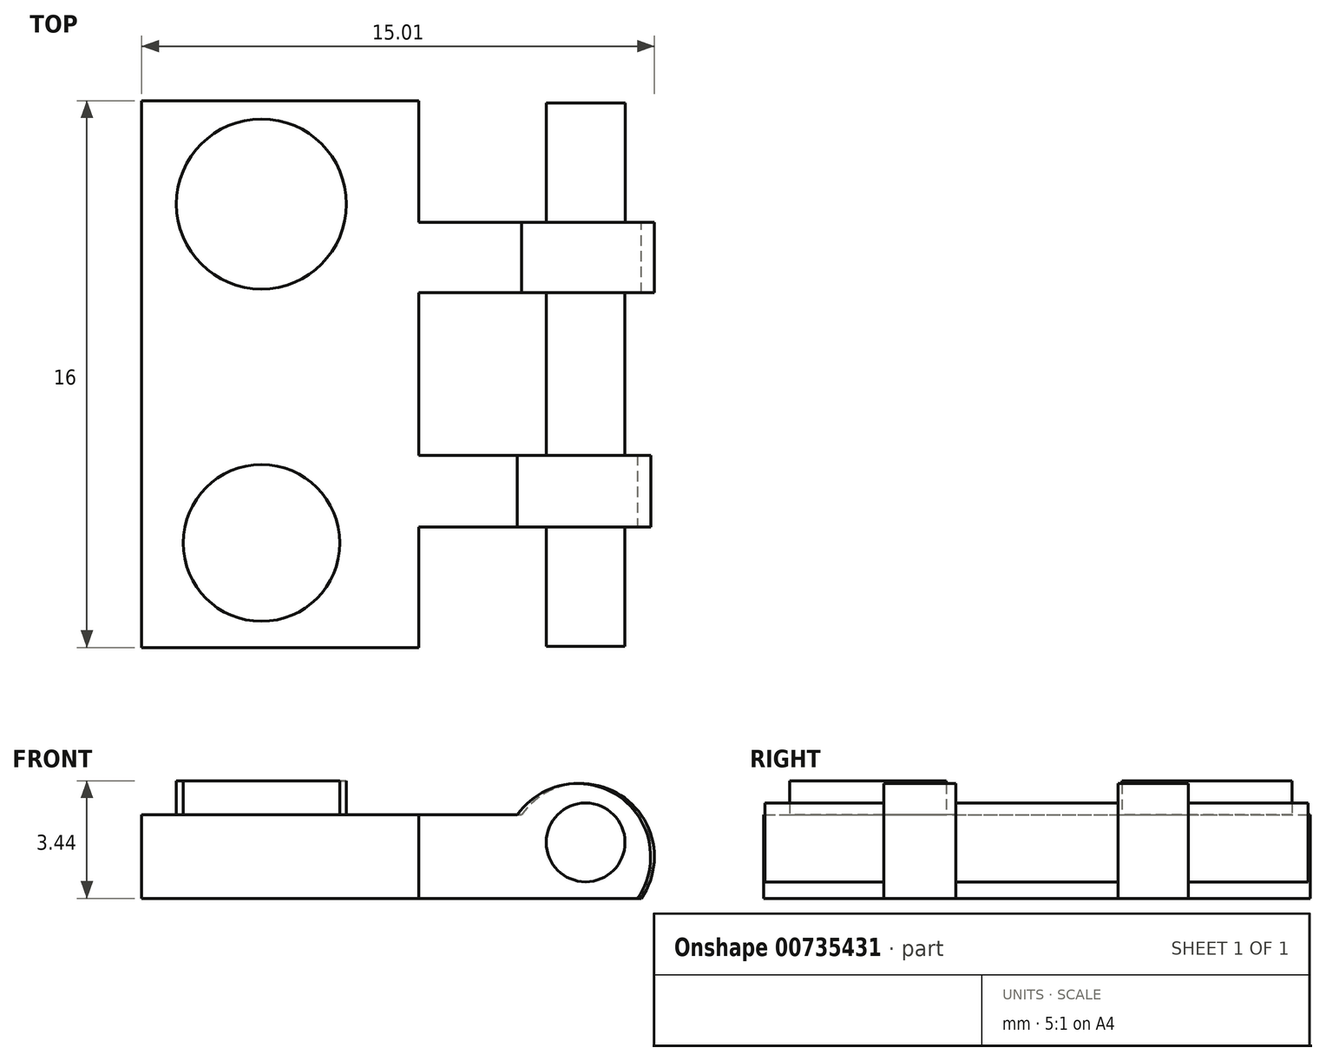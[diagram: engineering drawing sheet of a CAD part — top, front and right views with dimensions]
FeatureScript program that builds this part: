
annotation { "Feature Type Name" : "Feature", "Feature Type Description" : "" }
export const myFeature = defineFeature(function(context is Context, id is Id, definition is map)
    precondition{}
    {
        {
            var Q0;
            Q0=qCreatedBy(makeId("Front.planeOp"),FACE);
            var sketch = newSketch(context, id + "F0", { "sketchPlane" : qUnion([Q0])});
            skLineSegment(sketch, "E0", {"start": v(0, 0) * mm, "end": v(0, 2.44) * mm});
            skLineSegment(sketch, "E1", {"start": v(0, 2.44) * mm, "end": v(8.1, 2.44) * mm});
            skLineSegment(sketch, "E2", {"start": v(8.1, 2.44) * mm, "end": v(8.1, 0) * mm});
            skLineSegment(sketch, "E3", {"start": v(8.1, 0) * mm, "end": v(0, 0) * mm});
            skSolve(sketch);
        }
        {
            var Q0;
            Q0 = qSketchRegion(id + "F0", true);
            extrude(context, id + "F1", {"entities" : qUnion([Q0]), "depth" : 16 * mm, "offsetDistance" : 25 * mm});
        }
        {
            var Q0;
            Q0=makeQuery(id+"F1.opExtrude","SWEPT_FACE",FACE,{"disambiguationData":[OSD([sQuery(id+"F0.wireOp",EDGE,"E2")])]});
            var sketch = newSketch(context, id + "F2", { "sketchPlane" : qUnion([Q0])});
            skLineSegment(sketch, "E4", {"start": v(-12.48, 2.44) * mm, "end": v(-10.37, 2.44) * mm});
            skLineSegment(sketch, "E5", {"start": v(-3.56, 2.44) * mm, "end": v(-5.62, 2.44) * mm});
            skLineSegment(sketch, "E6", {"start": v(-12.48, 2.44) * mm, "end": v(-12.48, 0) * mm});
            skLineSegment(sketch, "E7", {"start": v(-12.48, 0) * mm, "end": v(-10.37, 0) * mm});
            skLineSegment(sketch, "E8", {"start": v(-10.37, 0) * mm, "end": v(-10.37, 2.44) * mm});
            skLineSegment(sketch, "E9", {"start": v(-5.62, 2.44) * mm, "end": v(-5.62, 0) * mm});
            skLineSegment(sketch, "E10", {"start": v(-5.62, 0) * mm, "end": v(-3.56, 0) * mm});
            skLineSegment(sketch, "E11", {"start": v(-3.56, 0) * mm, "end": v(-3.56, 2.44) * mm});
            skSolve(sketch);
        }
        {
            var Q0;
            Q0 = qSketchRegion(id + "F2", true);
            extrude(context, id + "F3", {"entities" : qUnion([Q0]), "operationType" : NewBodyOperationType.ADD, "depth" : 2.5 * mm, "offsetDistance" : 25 * mm});
        }
        {
            var Q0;
            Q0=makeQuery(id+"F3.opExtrude","SWEPT_FACE",FACE,{"disambiguationData":[OSD([sQuery(id+"F2.wireOp",EDGE,"E6")])]});
            var sketch = newSketch(context, id + "F4", { "sketchPlane" : qUnion([Q0])});
            skPoint(sketch, "E12.endSnap0", {"position": v(10.6, 1.22) * mm});
            skArc(sketch, "E13", {"start": v(14.52, 0) * mm, "mid": v(13.98, 2.98) * mm, "end": v(11, 2.44) * mm});
            skLineSegment(sketch, "E14", {"start": v(10.6, 0) * mm, "end": v(14.52, 0) * mm});
            skLineSegment(sketch, "E15", {"start": v(10.6, 2.44) * mm, "end": v(11, 2.44) * mm});
            skSolve(sketch);
        }
        {
            var Q0;
            Q0 = qSketchRegion(id + "F4", true);
            var Q1;
            Q1=makeQuery(id+"F4.imprint","IMPRINT",FACE,{"disambiguationData":[TD([[makeQuery(id+"F4.imprint","IMPRINT",EDGE,{"derivedFrom":sQuery(id+"F4.wireOp",EDGE,"E13")}),1.0]])]});
            extrude(context, id + "F5", {"entities" : qUnion([Q0, Q1]), "operationType" : NewBodyOperationType.ADD, "oppositeDirection" : true, "depth" : 2.1 * mm, "offsetDistance" : 25 * mm});
        }
        {
            var Q0;
            Q0=makeQuery(id+"F3.opExtrude","SWEPT_FACE",FACE,{"disambiguationData":[OSD([sQuery(id+"F2.wireOp",EDGE,"E11")])]});
            var sketch = newSketch(context, id + "F6", { "sketchPlane" : qUnion([Q0])});
            skPoint(sketch, "E16.endSnap0", {"position": v(8.94, -90.2) * mm});
            skArc(sketch, "E17", {"start": v(12.86, -91.43) * mm, "mid": v(12.32, -88.45) * mm, "end": v(9.34, -88.99) * mm});
            skLineSegment(sketch, "E18", {"start": v(8.94, -91.43) * mm, "end": v(12.86, -91.43) * mm});
            skLineSegment(sketch, "E19", {"start": v(8.94, -88.99) * mm, "end": v(9.34, -88.99) * mm});
            skArc(sketch, "E20", {"start": v(-11.12, 2.44) * mm, "mid": v(-14.1, 2.97) * mm, "end": v(-14.63, 0) * mm});
            skLineSegment(sketch, "E21", {"start": v(-10.6, 0) * mm, "end": v(-14.63, 0) * mm});
            skLineSegment(sketch, "E22", {"start": v(-10.6, 2.44) * mm, "end": v(-11.12, 2.44) * mm});
            skLineSegment(sketch, "E23", {"start": v(-10.6, 2.44) * mm, "end": v(-10.6, 0) * mm});
            skSolve(sketch);
        }
        {
            var Q0;
            Q0 = qSketchRegion(id + "F6", true);
            extrude(context, id + "F7", {"entities" : qUnion([Q0]), "operationType" : NewBodyOperationType.ADD, "oppositeDirection" : true, "depth" : 2.06 * mm, "offsetDistance" : 25 * mm});
        }
        {
            var Q0;
            Q0=makeQuery(id+"F7.boolean.opBoolean","MERGE",FACE,{"derivedFrom":[makeQuery(id+"F3.opExtrude","SWEPT_FACE",FACE,{"disambiguationData":[OSD([sQuery(id+"F2.wireOp",EDGE,"E11")])]}),makeQuery(id+"F7.opExtrude","CAP_FACE",FACE,{"disambiguationData":[OSD([sQuery(id+"F6.wireOp",EDGE,"E20"),sQuery(id+"F6.wireOp",EDGE,"E21"),sQuery(id+"F6.wireOp",EDGE,"E22"),sQuery(id+"F6.wireOp",EDGE,"E23")])],"isStart":true})]});
            var sketch = newSketch(context, id + "F8", { "sketchPlane" : qUnion([Q0])});
            skCircle(sketch, "E24", {"center": v(-13, 1.64) * mm, "radius": 1.16 * mm});
            skSolve(sketch);
        }
        {
            var Q0;
            Q0 = qSketchRegion(id + "F8", true);
            extrude(context, id + "F9", {"entities" : qUnion([Q0]), "operationType" : NewBodyOperationType.ADD, "depth" : 3.5 * mm, "offsetDistance" : 25 * mm});
        }
        {
            var Q0;
            Q0=makeQuery(id+"F7.boolean.opBoolean","MERGE",FACE,{"derivedFrom":[makeQuery(id+"F3.opExtrude","SWEPT_FACE",FACE,{"disambiguationData":[OSD([sQuery(id+"F2.wireOp",EDGE,"E11")])]}),makeQuery(id+"F7.opExtrude","CAP_FACE",FACE,{"disambiguationData":[OSD([sQuery(id+"F6.wireOp",EDGE,"E20"),sQuery(id+"F6.wireOp",EDGE,"E21"),sQuery(id+"F6.wireOp",EDGE,"E22"),sQuery(id+"F6.wireOp",EDGE,"E23")])],"isStart":true})]});
            var sketch = newSketch(context, id + "F10", { "sketchPlane" : qUnion([Q0])});
            skCircle(sketch, "E25", {"center": v(-13, 1.64) * mm, "radius": 1.15 * mm});
            skSolve(sketch);
        }
        {
            var Q0;
            Q0 = qSketchRegion(id + "F10", true);
            extrude(context, id + "F11", {"entities" : qUnion([Q0]), "operationType" : NewBodyOperationType.ADD, "oppositeDirection" : true, "depth" : 12.4 * mm, "offsetDistance" : 25 * mm});
        }
        {
            var Q0;
            Q0=makeQuery(id+"F7.boolean.opBoolean","MERGE",FACE,{"derivedFrom":[makeQuery(id+"F5.boolean.opBoolean","MERGE",FACE,{"derivedFrom":[makeQuery(id+"F3.boolean.opBoolean","MERGE",FACE,{"derivedFrom":[makeQuery(id+"F1.opExtrude","SWEPT_FACE",FACE,{"disambiguationData":[OSD([sQuery(id+"F0.wireOp",EDGE,"E1")])]}),makeQuery(id+"F3.opExtrude","SWEPT_FACE",FACE,{"disambiguationData":[OSD([sQuery(id+"F2.wireOp",EDGE,"E4")])]}),makeQuery(id+"F3.opExtrude","SWEPT_FACE",FACE,{"disambiguationData":[OSD([sQuery(id+"F2.wireOp",EDGE,"E5")])]})]}),makeQuery(id+"F5.opExtrude","SWEPT_FACE",FACE,{"disambiguationData":[OSD([sQuery(id+"F4.wireOp",EDGE,"E15")])]})]}),makeQuery(id+"F7.opExtrude","SWEPT_FACE",FACE,{"disambiguationData":[OSD([sQuery(id+"F6.wireOp",EDGE,"E22")])]})]});
            var sketch = newSketch(context, id + "F12", { "sketchPlane" : qUnion([Q0])});
            skCircle(sketch, "E26", {"center": v(3.5, -12.94) * mm, "radius": 2.3 * mm});
            skCircle(sketch, "E27", {"center": v(3.5, -3.02) * mm, "radius": 2.49 * mm});
            skSolve(sketch);
        }
        {
            var Q0;
            Q0 = qSketchRegion(id + "F12", true);
            extrude(context, id + "F13", {"entities" : qUnion([Q0]), "operationType" : NewBodyOperationType.ADD, "depth" : 1 * mm, "offsetDistance" : 25 * mm});
        }
    });
